# Revit family: FU   Fam-Elektro
name_source: partatom
category: Electrical Fixtures
revit_build: Autodesk Revit 2016 (Build: 20150714_1515(x64)
units: mm (PartAtom-declared; Revit-internal decimal feet)

## family parameters
Always vertical = Yes
Cut with Voids When Loaded = No
Maintain Annotation Orientation = No
OmniClass Number = 23.80.00.00
OmniClass Title = Electric Power and Lighting
Part Type = Normal
Room Calculation Point = No
Round Connector Dimension = Use Diameter
Shared = No
Work Plane-Based = No

## types (12) — shared parameters
Edition number = 1
IFC Classification = Electric Distribution
Manufacturer = Siemens AG
Product Guid = e03dd065-3347-4e71-9716-9838e1e99805
Product data url = https://bimobject.com
T = 600 mm

## per-type parameters (varying)
| type | B | H | Model | Rated Power / Rated Voltage |
| Cabinet VFD G150  800x 600x2000  IP20 | 800 mm  [stored 2.62467 ft] | 2000 mm  [stored 6.56168 ft] | Cabinet VFD G150  800x 600x2000  IP20 | 110-160kW/380-480V & 110-200kW/500-600V & 75-315kW/660-690V, for Application: Moving, Processing
110-160kW/380-480V & 110-200kW/500-600V & 75-315kW/660-690V, for Application: Moving, Processing |
| Cabinet VFD G150 1000x 600x2000  IP20 | 1000 mm  [stored 3.28084 ft] | 2000 mm  [stored 6.56168 ft] | Cabinet VFD G150 1000x 600x2000  IP20 | 200-250kW/380-480V,  for Application: Moving, Processing |
| Cabinet VFD G150 1200x 600x2000  IP20 | 1200 mm  [stored 3.93701 ft] | 2000 mm  [stored 6.56168 ft] | Cabinet VFD G150 1200x 600x2000  IP20 | 315-450kW/380-480V & 250-400kW/500-600V &400-560kW/660-690V, for Application: Moving, Processing |
| Cabinet VFD G150 1600x 600x2000  IP20 | 1600 mm  [stored 5.24934 ft] | 2000 mm  [stored 6.56168 ft] | Cabinet VFD G150 1600x 600x2000  IP20 | 560kW/380-480V & 500-560kW/500-600V & 710-800kW/660V-690V, for Application: Moving, Processing |
| Cabinet VFD G120P 1000x 600x2300  IP20 | 1000 mm  [stored 3.28084 ft] | 2300 mm | Cabinet VFD G120P 1000x 600x2300  IP20 | 110-250kW/380-480V, für Applikation: Pumping, Ventilation, Compressing |
| Cabinet VFD G120P 1200x 600x2300  IP20 | 1200 mm  [stored 3.93701 ft] | 2300 mm | Cabinet VFD G120P 1200x 600x2300  IP20 | 315-560kW/380-480V & 500-630kW/500-690V, Pumping, Ventilation, Compressing |
| Cabinet VFD G120P 1000x 600x2400  IP43 | 1000 mm  [stored 3.28084 ft] | 2400 mm | Cabinet VFD G120P 1000x 600x2400  IP43 | 110-250kW/380-480V, für Applikation: Pumping, Ventilation, Compressing |
| Cabinet VFD G120P 1200x 600x2400  IP43 | 1200 mm  [stored 3.93701 ft] | 2400 mm | Cabinet VFD G120P 1200x 600x2400  IP43 | 315-560kW/380-480V & 500-630kW/500-690V, Pumping, Ventilation, Compressing |
| Cabinet VFD G150  800x 600x2400  IP43 | 800 mm  [stored 2.62467 ft] | 2400 mm | Cabinet VFD G150  800x 600x2400  IP43 | 110-160kW/380-480V & 110-200kW/500-600V & 75-315kW/660-690V, for Application: Moving, Processing
110-160kW/380-480V & 110-200kW/500-600V & 75-315kW/660-690V, for Application: Moving, Processing |
| Cabinet VFD G150 1000x 600x2400 IP43 | 1000 mm  [stored 3.28084 ft] | 2400 mm | Cabinet VFD G150 1000x 600x2000  IP43 | 200-250kW/380-480V,  for Application: Moving, Processing |
| Cabinet VFD G150 1200x 600x2400  IP43 | 1200 mm  [stored 3.93701 ft] | 2400 mm | Cabinet VFD G150 1200x 600x2000  IP43 | 315-450kW/380-480V & 250-400kW/500-600V &400-560kW/660-690V, for Application: Moving, Processing |
| Cabinet VFD G150 1600x 600x2400  IP43 | 1600 mm  [stored 5.24934 ft] | 2400 mm | Cabinet VFD G150 1600x 600x2000  IP43 | 560kW/380-480V & 500-560kW/500-600V & 710-800kW/660V-690V, for Application: Moving, Processing |

note: [stored X ft] marks values corroborated as IEEE doubles in the binary element streams (Revit-internal decimal feet)

## geometry (parser evidence)
native form markers: Blend x12
no freeform markers — native parametric forms only
